# Revit family: Faucet-Valve_Trim-KOHLER-Honesty-K-TS99761-4
name_source: partatom
category: Generic Models
revit_build: Autodesk Revit 2015 (Build: 20140606_1530(x64)
units: mm (PartAtom-declared; Revit-internal decimal feet)

## types (1)
- CP-Polished Chrome
    ADA Compliant = Yes
    Assembly Code = C1030200
    Date Modified = 09/07/2017
    Default Elevation = 42"
    Description = Honesty Rite-Temp Valve Trim with Diverter
    Finish = Kohler-Metal-CP-Polished_Chrome
    Height = 4 1/2"
    Inlet Connector = Inlet Connection
    Length = 6 1/2"
    Manufacturer = Kohler
    MasterFormat 1995 = 10820
    MasterFormat 2004 = 10.28.13
    Material = Premium Construction
    Model = K-TS99761-4-CP
    Outlet Connector = Outlet Connection
    Product Documentation Link = http://www.us.kohler.com
    Product Name = Honesty
    Product Page URL = http://www.us.kohler.com
    Type = 1
    URL = http://www.us.kohler.com
    Waste Connection = Yes
    Width = 6 1/2"

## geometry (parser evidence)
native form markers: Sweep x6
no freeform markers — native parametric forms only
